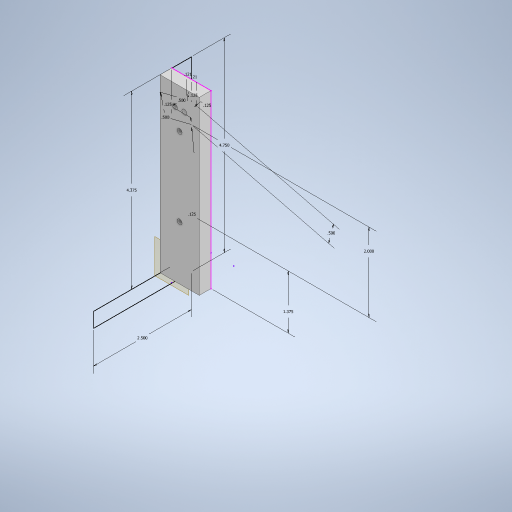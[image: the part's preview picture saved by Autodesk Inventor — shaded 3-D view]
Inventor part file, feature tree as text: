
AUTODESK INVENTOR PART (.ipt)
format: ipt  version: 2023 (Build 270158000, 158)  size: 266,240 bytes
history: native  units: in
note: dims shown in document units (in); Inventor stores cm internally (conversion verified against a paired STEP export)
features: sketch x2, plane x1, extrude x1
ambient origin geometry x8: Origin, YZ Plane, XZ Plane, XY Plane, X Axis, Y Axis, Z Axis, Center Point
bodies: Body1 (feature_tree)
feature tree (4):
  sketch  "Sketch1"  dims[d0=4.375in d1=0.5in]
  plane  "Work Plane1"
  sketch  "Sketch2"  dims[d2=4.75in d3=2.5in d7=0.125in d8=0.125in d9=1.375in d10=2.0in d11=0.125in d12=0.5in d17=0.125in d18=0.5in d22=0.1213in d23=0.1213in d30=0.3in d31=0.0in]
  extrude  "Extrusion4"  Depth=4.375in
